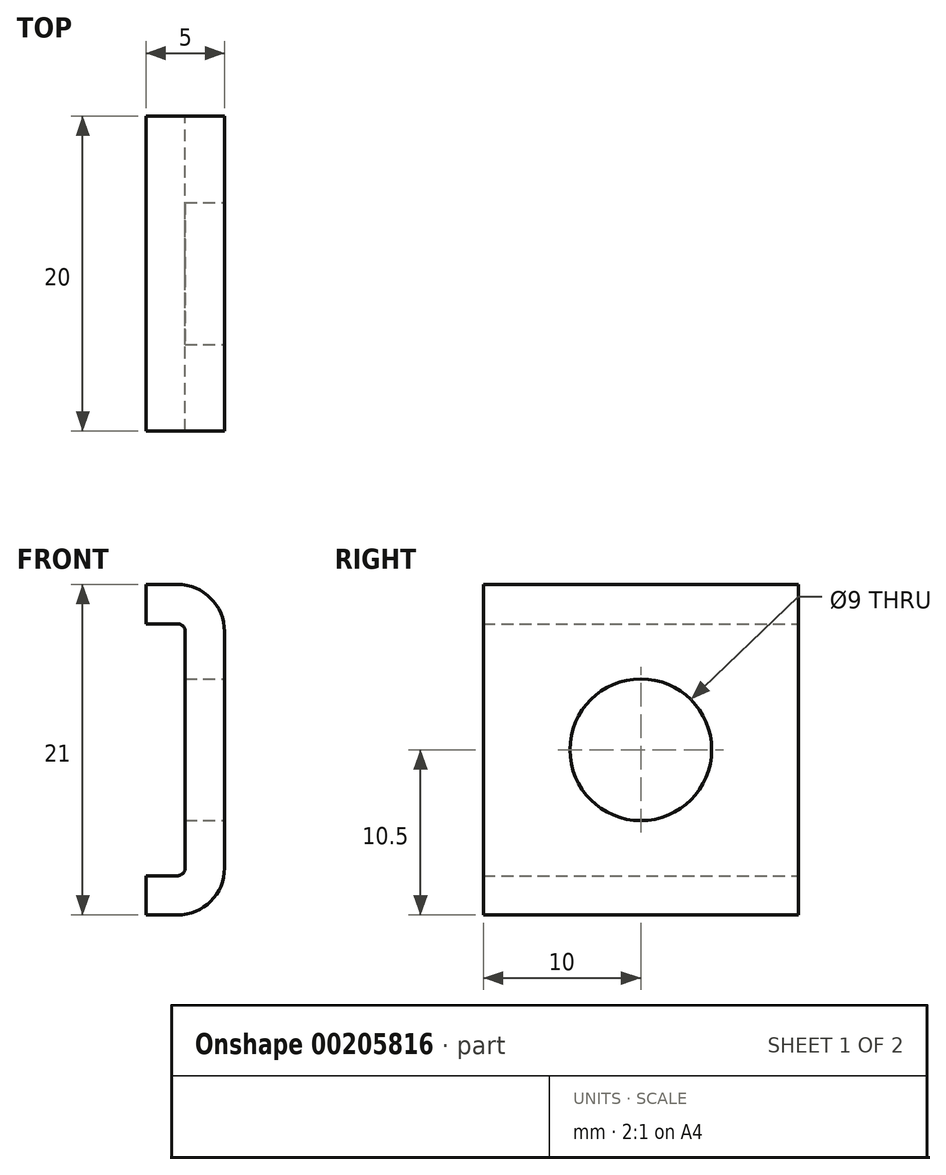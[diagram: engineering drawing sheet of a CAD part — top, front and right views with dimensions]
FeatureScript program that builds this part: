
annotation { "Feature Type Name" : "Feature", "Feature Type Description" : "" }
export const myFeature = defineFeature(function(context is Context, id is Id, definition is map)
    precondition{}
    {
        {
            var Q0;
            Q0=qCreatedBy(makeId("Front.planeOp"),FACE);
            var sketch = newSketch(context, id + "F0", { "sketchPlane" : qUnion([Q0])});
            skLineSegment(sketch, "E0", {"start": v(2.5, 0) * mm, "end": v(2.5, 7.5) * mm});
            skLineSegment(sketch, "E1", {"start": v(-0.5, 10.5) * mm, "end": v(-2.5, 10.5) * mm});
            skLineSegment(sketch, "E2", {"start": v(-2.5, 10.5) * mm, "end": v(-2.5, 8) * mm});
            skLineSegment(sketch, "E3", {"start": v(-2.5, 8) * mm, "end": v(-0.5, 8) * mm});
            skLineSegment(sketch, "E4", {"start": v(0, 7.5) * mm, "end": v(0, 0) * mm});
            skLineSegment(sketch, "E5", {"start": v(0, 0) * mm, "end": v(2.5, 0) * mm});
            skPoint(sketch, "E6.visualSharp", {"position": v(0, 8) * mm});
            skArc(sketch, "E6.filletArc", {"start": v(0, 7.5) * mm, "mid": v(-0.15, 7.85) * mm, "end": v(-0.5, 8) * mm});
            skPoint(sketch, "E7.visualSharp", {"position": v(2.5, 10.5) * mm});
            skArc(sketch, "E7.filletArc", {"start": v(2.5, 7.5) * mm, "mid": v(1.62, 9.62) * mm, "end": v(-0.5, 10.5) * mm});
            skSolve(sketch);
        }
        {
            var Q0;
            Q0=makeQuery(id+"F0.imprint","IMPRINT",FACE,{"disambiguationData":[TD([[makeQuery(id+"F0.imprint","IMPRINT",EDGE,{"derivedFrom":sQuery(id+"F0.wireOp",EDGE,"E0")}),1.0]])]});
            extrude(context, id + "F1", {"entities" : qUnion([Q0]), "depth" : 10 * mm, "hasSecondDirection" : true, "secondDirectionOppositeDirection" : true, "secondDirectionDepth" : 10 * mm});
        }
        {
            var Q0;
            Q0=makeQuery(id+"F1.opExtrude","SWEPT_BODY",BODY,{"disambiguationData":[OSD([sQuery(id+"F0.wireOp",EDGE,"E0"),sQuery(id+"F0.wireOp",EDGE,"E1"),sQuery(id+"F0.wireOp",EDGE,"E2"),sQuery(id+"F0.wireOp",EDGE,"E3"),sQuery(id+"F0.wireOp",EDGE,"E4"),sQuery(id+"F0.wireOp",EDGE,"E5"),sQuery(id+"F0.wireOp",EDGE,"E6.filletArc"),sQuery(id+"F0.wireOp",EDGE,"E7.filletArc")])]});
            var Q1;
            Q1=makeQuery(id+"F1.opExtrude","SWEPT_FACE",FACE,{"disambiguationData":[OSD([sQuery(id+"F0.wireOp",EDGE,"E5")])]});
            mirror(context, id + "F2", {"operationType" : NewBodyOperationType.ADD, "entities" : qUnion([Q0]), "mirrorPlane" : qUnion([Q1])});
        }
        {
            var Q0;
            {var subQ0=makeQuery(id+"F1.opExtrude","SWEPT_FACE",FACE,{"disambiguationData":[OSD([sQuery(id+"F0.wireOp",EDGE,"E0")])]});Q0=makeQuery(id+"F2.boolean.opBoolean","MERGE",FACE,{"derivedFrom":[subQ0,makeQuery(id+"F2.opPattern","COPY",FACE,{"derivedFrom":subQ0,"instanceName":"1"})]});}
            var sketch = newSketch(context, id + "F3", { "sketchPlane" : qUnion([Q0])});
            skPoint(sketch, "E8", {"position": v(0, 0) * mm});
            skSolve(sketch);
        }
        {
            var Q0;
            Q0=sQuery(id+"F3.wireOp",VERTEX,"E8");
            var Q1;
            Q1=makeQuery(id+"F1.opExtrude","SWEPT_BODY",BODY,{"disambiguationData":[OSD([sQuery(id+"F0.wireOp",EDGE,"E0"),sQuery(id+"F0.wireOp",EDGE,"E1"),sQuery(id+"F0.wireOp",EDGE,"E2"),sQuery(id+"F0.wireOp",EDGE,"E3"),sQuery(id+"F0.wireOp",EDGE,"E4"),sQuery(id+"F0.wireOp",EDGE,"E5"),sQuery(id+"F0.wireOp",EDGE,"E6.filletArc"),sQuery(id+"F0.wireOp",EDGE,"E7.filletArc")])]});
            hole(context, id + "F4", {"style" : HoleStyle.SIMPLE, "endStyle" : HoleEndStyle.THROUGH, "holeDiameter" : 9 * mm, "locations" : qUnion([Q0]), "scope" : qUnion([Q1]), "isTappedThrough" : true});
        }
    });
